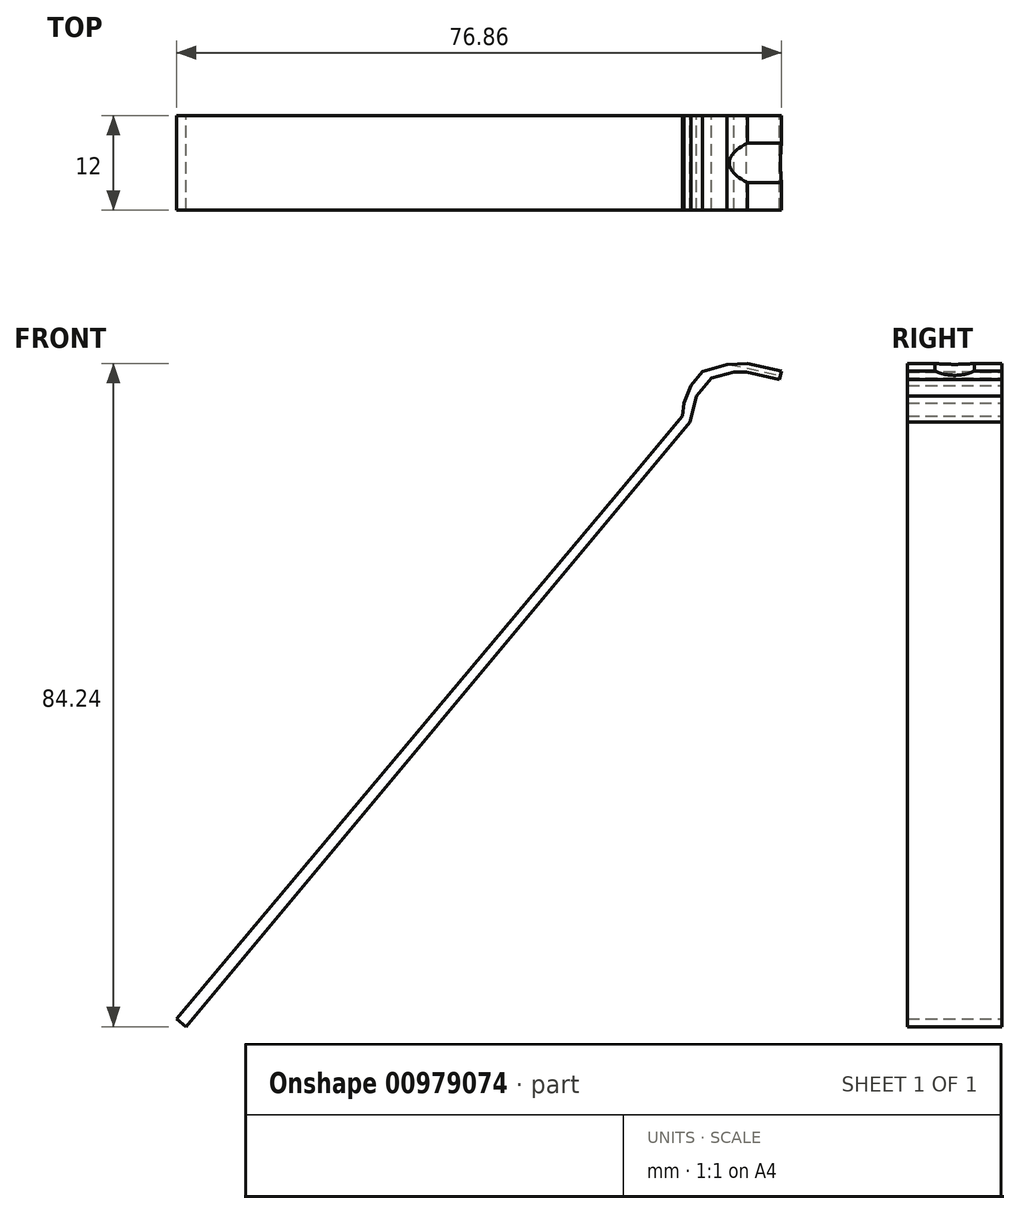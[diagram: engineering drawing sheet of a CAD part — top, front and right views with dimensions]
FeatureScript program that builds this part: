
annotation { "Feature Type Name" : "Feature", "Feature Type Description" : "" }
export const myFeature = defineFeature(function(context is Context, id is Id, definition is map)
    precondition{}
    {
        {
            var Q0;
            Q0=qCreatedBy(makeId("Front.planeOp"),FACE);
            var sketch = newSketch(context, id + "F0", { "sketchPlane" : qUnion([Q0])});
            skLineSegment(sketch, "E0", {"start": v(44.06, 58.42) * mm, "end": v(50.46, 66.1) * mm});
            skLineSegment(sketch, "E1", {"start": v(50.46, 66.1) * mm, "end": v(51.3, 69.4) * mm});
            skLineSegment(sketch, "E2", {"start": v(51.3, 69.4) * mm, "end": v(53.23, 71.65) * mm});
            skLineSegment(sketch, "E3", {"start": v(53.23, 71.65) * mm, "end": v(56.07, 72.42) * mm});
            skLineSegment(sketch, "E4", {"start": v(56.07, 72.42) * mm, "end": v(57.68, 72.42) * mm});
            skLineSegment(sketch, "E5", {"start": v(57.68, 72.42) * mm, "end": v(61.87, 71.52) * mm});
            skLineSegment(sketch, "E6", {"start": v(61.87, 71.52) * mm, "end": v(62.1, 72.58) * mm});
            skLineSegment(sketch, "E7", {"start": v(62.1, 72.58) * mm, "end": v(57.75, 73.52) * mm});
            skLineSegment(sketch, "E8", {"start": v(57.75, 73.52) * mm, "end": v(55.18, 73.41) * mm});
            skLineSegment(sketch, "E9", {"start": v(55.18, 73.41) * mm, "end": v(52.09, 72.5) * mm});
            skLineSegment(sketch, "E10", {"start": v(52.09, 72.5) * mm, "end": v(50.6, 70.7) * mm});
            skLineSegment(sketch, "E11", {"start": v(50.6, 70.7) * mm, "end": v(49.7, 68.51) * mm});
            skLineSegment(sketch, "E12", {"start": v(49.7, 68.51) * mm, "end": v(49.51, 66.84) * mm});
            skLineSegment(sketch, "E13", {"start": v(49.51, 66.84) * mm, "end": v(43.14, 59.2) * mm});
            skLineSegment(sketch, "E14", {"start": v(43.14, 59.2) * mm, "end": v(44.06, 58.42) * mm});
            skLineSegment(sketch, "E15", {"start": v(44.06, 58.42) * mm, "end": v(-13.56, -10.72) * mm});
            skLineSegment(sketch, "E16", {"start": v(-13.56, -10.72) * mm, "end": v(-14.76, -9.72) * mm});
            skLineSegment(sketch, "E17", {"start": v(-14.76, -9.72) * mm, "end": v(43.14, 59.2) * mm});
            skSolve(sketch);
        }
        {
            var Q0;
            Q0 = qSketchRegion(id + "F0", true);
            extrude(context, id + "F1", {"entities" : qUnion([Q0]), "depth" : 12 * mm, "offsetDistance" : 25 * mm});
        }
        {
            var Q0;
            Q0=makeQuery(id+"F1.opExtrude","SWEPT_FACE",FACE,{"disambiguationData":[OSD([sQuery(id+"F0.wireOp",EDGE,"E6")])]});
            var sketch = newSketch(context, id + "F2", { "sketchPlane" : qUnion([Q0])});
            skCircle(sketch, "E18", {"center": v(-6, 89.15) * mm, "radius": 5.7 * mm});
            skPoint(sketch, "E18.centerSnap0", {"position": v(-6, 84.03) * mm});
            skSolve(sketch);
        }
        {
            var Q0;
            Q0 = qSketchRegion(id + "F2", true);
            extrude(context, id + "F3", {"entities" : qUnion([Q0]), "operationType" : NewBodyOperationType.REMOVE, "oppositeDirection" : true, "depth" : 25 * mm, "offsetDistance" : 25 * mm});
        }
    });
